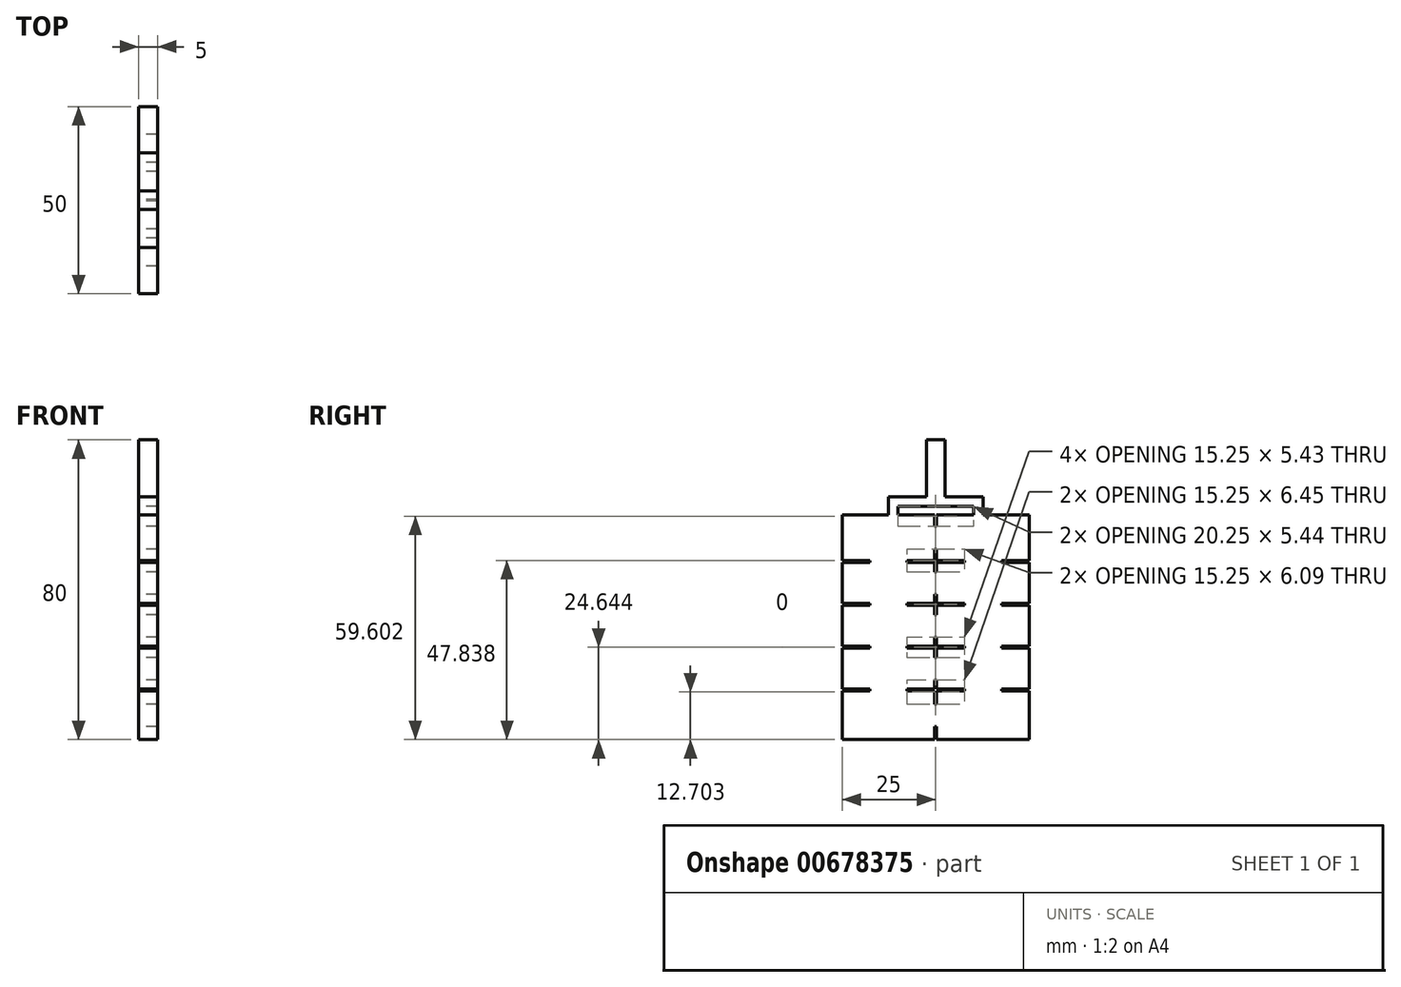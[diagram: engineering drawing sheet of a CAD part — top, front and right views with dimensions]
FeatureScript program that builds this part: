
annotation { "Feature Type Name" : "Feature", "Feature Type Description" : "" }
export const myFeature = defineFeature(function(context is Context, id is Id, definition is map)
    precondition{}
    {
        {
            var Q0;
            Q0=qCreatedBy(makeId("Right.planeOp"),FACE);
            var sketch = newSketch(context, id + "F0", { "sketchPlane" : qUnion([Q0])});
            skPoint(sketch, "E0.0", {"position": v(0, 0) * mm});
            skLineSegment(sketch, "E1.bottom", {"start": v(0, 0) * mm, "end": v(12.38, 0) * mm});
            skLineSegment(sketch, "E1.top", {"start": v(0, -60) * mm, "end": v(24.75, -60) * mm});
            skLineSegment(sketch, "E1.left", {"start": v(0, 0) * mm, "end": v(0, -12.24) * mm});
            skLineSegment(sketch, "E1.right", {"start": v(50, 0) * mm, "end": v(50, -12.24) * mm});
            skPoint(sketch, "E2.MirrorP", {"position": v(11.5, 0) * mm});
            skPoint(sketch, "E3.MirrorP", {"position": v(11.5, -2) * mm});
            skPoint(sketch, "E4.MirrorP", {"position": v(18.5, 0) * mm});
            skPoint(sketch, "E5.MirrorP", {"position": v(30, 0) * mm});
            skLineSegment(sketch, "E6.0", {"start": v(25.25, -60) * mm, "end": v(25.25, -56.52) * mm});
            skLineSegment(sketch, "E7.0", {"start": v(0, -12.24) * mm, "end": v(7.38, -12.24) * mm});
            skLineSegment(sketch, "E8.0", {"start": v(0, -12.74) * mm, "end": v(7.38, -12.74) * mm});
            skLineSegment(sketch, "E9.trimOffspring", {"start": v(25.25, -3.12) * mm, "end": v(25.25, -1.3) * mm});
            skLineSegment(sketch, "E10.trimOffspring", {"start": v(25.25, -12.24) * mm, "end": v(32.63, -12.24) * mm});
            skLineSegment(sketch, "E11.trimOffspring", {"start": v(25.25, -12.24) * mm, "end": v(25.25, -9.12) * mm});
            skLineSegment(sketch, "E12.trimOffspring", {"start": v(25.25, -12.74) * mm, "end": v(32.63, -12.74) * mm});
            skLineSegment(sketch, "E13.trimOffspring", {"start": v(25.25, -15.2) * mm, "end": v(25.25, -12.74) * mm});
            skLineSegment(sketch, "E14.0", {"start": v(0, -23.67) * mm, "end": v(7.38, -23.67) * mm});
            skLineSegment(sketch, "E15.0", {"start": v(0, -24.17) * mm, "end": v(7.38, -24.17) * mm});
            skLineSegment(sketch, "E16.trimOffspring", {"start": v(25.25, -23.67) * mm, "end": v(32.63, -23.67) * mm});
            skLineSegment(sketch, "E17.trimOffspring", {"start": v(25.25, -23.67) * mm, "end": v(25.25, -21.2) * mm});
            skLineSegment(sketch, "E18.trimOffspring", {"start": v(25.25, -24.17) * mm, "end": v(32.63, -24.17) * mm});
            skLineSegment(sketch, "E19.trimOffspring", {"start": v(25.25, -26.64) * mm, "end": v(25.25, -24.17) * mm});
            skLineSegment(sketch, "E20.trimOffspring", {"start": v(24.75, -26.64) * mm, "end": v(24.75, -24.17) * mm});
            skLineSegment(sketch, "E21.0", {"start": v(0, -35.1) * mm, "end": v(7.38, -35.1) * mm});
            skLineSegment(sketch, "E22.0", {"start": v(0, -35.6) * mm, "end": v(7.38, -35.6) * mm});
            skLineSegment(sketch, "E23.trimOffspring", {"start": v(25.25, -35.1) * mm, "end": v(32.63, -35.1) * mm});
            skLineSegment(sketch, "E24.trimOffspring", {"start": v(25.25, -35.1) * mm, "end": v(25.25, -32.64) * mm});
            skLineSegment(sketch, "E25.trimOffspring", {"start": v(24.75, -35.1) * mm, "end": v(24.75, -32.64) * mm});
            skLineSegment(sketch, "E26.trimOffspring", {"start": v(25.25, -35.6) * mm, "end": v(32.63, -35.6) * mm});
            skLineSegment(sketch, "E27.trimOffspring", {"start": v(25.25, -38.07) * mm, "end": v(25.25, -35.6) * mm});
            skLineSegment(sketch, "E28.trimOffspring", {"start": v(24.75, -38.07) * mm, "end": v(24.75, -35.6) * mm});
            skLineSegment(sketch, "E29.0", {"start": v(0, -46.54) * mm, "end": v(7.38, -46.54) * mm});
            skLineSegment(sketch, "E30.0", {"start": v(0, -47.04) * mm, "end": v(7.38, -47.04) * mm});
            skLineSegment(sketch, "E31.trimOffspring", {"start": v(25.25, -46.54) * mm, "end": v(32.63, -46.54) * mm});
            skLineSegment(sketch, "E32.trimOffspring", {"start": v(25.25, -46.54) * mm, "end": v(25.25, -44.07) * mm});
            skLineSegment(sketch, "E33.trimOffspring", {"start": v(24.75, -46.54) * mm, "end": v(24.75, -44.07) * mm});
            skLineSegment(sketch, "E34.trimOffspring", {"start": v(25.25, -47.04) * mm, "end": v(32.63, -47.04) * mm});
            skLineSegment(sketch, "E35.trimOffspring", {"start": v(25.25, -50.52) * mm, "end": v(25.25, -47.04) * mm});
            skLineSegment(sketch, "E36.trimOffspring", {"start": v(0, -12.74) * mm, "end": v(0, -23.67) * mm});
            skLineSegment(sketch, "E37.trimOffspring", {"start": v(0, -24.17) * mm, "end": v(0, -35.1) * mm});
            skLineSegment(sketch, "E38.trimOffspring", {"start": v(0, -35.6) * mm, "end": v(0, -46.54) * mm});
            skLineSegment(sketch, "E39.trimOffspring", {"start": v(0, -47.04) * mm, "end": v(0, -60) * mm});
            skLineSegment(sketch, "E40.trimOffspring", {"start": v(50, -47.04) * mm, "end": v(50, -60) * mm});
            skLineSegment(sketch, "E41.trimOffspring", {"start": v(50, -35.6) * mm, "end": v(50, -46.54) * mm});
            skLineSegment(sketch, "E42.trimOffspring", {"start": v(50, -12.74) * mm, "end": v(50, -23.67) * mm});
            skLineSegment(sketch, "E43.trimOffspring", {"start": v(50, -24.17) * mm, "end": v(50, -35.1) * mm});
            skLineSegment(sketch, "E44.0", {"start": v(17.38, -12.74) * mm, "end": v(17.38, -12.24) * mm});
            skLineSegment(sketch, "E45.0", {"start": v(7.38, -12.74) * mm, "end": v(7.38, -12.24) * mm});
            skLineSegment(sketch, "E46", {"start": v(24.75, -12.24) * mm, "end": v(24.75, -9.12) * mm});
            skLineSegment(sketch, "E47.0", {"start": v(24.75, -9.12) * mm, "end": v(25.25, -9.12) * mm});
            skLineSegment(sketch, "E48.0", {"start": v(24.75, -3.12) * mm, "end": v(25.25, -3.12) * mm});
            skLineSegment(sketch, "E49", {"start": v(24.75, -12.74) * mm, "end": v(24.75, -15.2) * mm});
            skLineSegment(sketch, "E50.0", {"start": v(24.75, -21.2) * mm, "end": v(25.25, -21.2) * mm});
            skLineSegment(sketch, "E51.0", {"start": v(24.75, -15.2) * mm, "end": v(25.25, -15.2) * mm});
            skLineSegment(sketch, "E52", {"start": v(25.25, -1.3) * mm, "end": v(25.25, 0) * mm});
            skLineSegment(sketch, "E53.trimOffspring", {"start": v(25.25, 0) * mm, "end": v(35.12, 0) * mm});
            skPoint(sketch, "E54.start.orphan", {"position": v(24.75, -6.12) * mm});
            skLineSegment(sketch, "E55", {"start": v(7.38, -12.24) * mm, "end": v(7.38, -12.74) * mm});
            skLineSegment(sketch, "E56", {"start": v(17.38, -12.24) * mm, "end": v(17.38, -12.74) * mm});
            skLineSegment(sketch, "E57.trimOffspring", {"start": v(7.38, -23.67) * mm, "end": v(7.38, -24.17) * mm});
            skLineSegment(sketch, "E58.trimOffspring", {"start": v(17.38, -23.67) * mm, "end": v(17.38, -24.17) * mm});
            skLineSegment(sketch, "E59.trimOffspring", {"start": v(7.38, -35.1) * mm, "end": v(7.38, -35.6) * mm});
            skLineSegment(sketch, "E60.trimOffspring", {"start": v(17.38, -35.1) * mm, "end": v(17.38, -35.6) * mm});
            skLineSegment(sketch, "E61.trimOffspring", {"start": v(7.38, -46.54) * mm, "end": v(7.38, -47.04) * mm});
            skLineSegment(sketch, "E62.trimOffspring", {"start": v(17.38, -46.54) * mm, "end": v(17.38, -47.04) * mm});
            skLineSegment(sketch, "E63.trimOffspring", {"start": v(17.38, -46.54) * mm, "end": v(24.75, -46.54) * mm});
            skLineSegment(sketch, "E64.trimOffspring", {"start": v(17.38, -47.04) * mm, "end": v(24.75, -47.04) * mm});
            skLineSegment(sketch, "E65.trimOffspring", {"start": v(17.38, -35.1) * mm, "end": v(24.75, -35.1) * mm});
            skLineSegment(sketch, "E66.trimOffspring", {"start": v(17.38, -35.6) * mm, "end": v(24.75, -35.6) * mm});
            skLineSegment(sketch, "E67.trimOffspring", {"start": v(17.37, -23.67) * mm, "end": v(24.75, -23.67) * mm});
            skLineSegment(sketch, "E68.trimOffspring", {"start": v(17.37, -24.17) * mm, "end": v(24.75, -24.17) * mm});
            skLineSegment(sketch, "E69.trimOffspring", {"start": v(17.38, -12.24) * mm, "end": v(24.75, -12.24) * mm});
            skPoint(sketch, "E70.start.orphan", {"position": v(12.38, -12.74) * mm});
            skPoint(sketch, "E71.orphan", {"position": v(12.38, -12.24) * mm});
            skLineSegment(sketch, "E72.trimOffspring", {"start": v(17.38, -12.74) * mm, "end": v(24.75, -12.74) * mm});
            skLineSegment(sketch, "E73.0", {"start": v(32.63, -12.24) * mm, "end": v(32.63, -12.74) * mm});
            skLineSegment(sketch, "E74.0", {"start": v(42.62, -12.24) * mm, "end": v(42.62, -12.74) * mm});
            skLineSegment(sketch, "E75.trimOffspring", {"start": v(32.63, -23.67) * mm, "end": v(32.63, -24.17) * mm});
            skLineSegment(sketch, "E76.trimOffspring", {"start": v(42.62, -23.67) * mm, "end": v(42.62, -24.17) * mm});
            skLineSegment(sketch, "E77.trimOffspring", {"start": v(32.63, -35.1) * mm, "end": v(32.63, -35.6) * mm});
            skLineSegment(sketch, "E78.trimOffspring", {"start": v(42.62, -35.1) * mm, "end": v(42.62, -35.6) * mm});
            skLineSegment(sketch, "E79.trimOffspring", {"start": v(32.63, -46.54) * mm, "end": v(32.63, -47.04) * mm});
            skLineSegment(sketch, "E80.trimOffspring", {"start": v(42.62, -46.54) * mm, "end": v(42.62, -47.04) * mm});
            skLineSegment(sketch, "E81.0", {"start": v(24.75, -26.64) * mm, "end": v(25.25, -26.64) * mm});
            skLineSegment(sketch, "E82.0", {"start": v(24.75, -32.64) * mm, "end": v(25.25, -32.64) * mm});
            skLineSegment(sketch, "E83.0", {"start": v(24.75, -38.07) * mm, "end": v(25.25, -38.07) * mm});
            skLineSegment(sketch, "E84.0", {"start": v(24.75, -44.07) * mm, "end": v(25.25, -44.07) * mm});
            skLineSegment(sketch, "E85", {"start": v(24.75, -47.04) * mm, "end": v(24.75, -50.52) * mm});
            skLineSegment(sketch, "E86.0", {"start": v(24.75, -56.52) * mm, "end": v(25.25, -56.52) * mm});
            skLineSegment(sketch, "E87.0", {"start": v(24.75, -50.52) * mm, "end": v(25.25, -50.52) * mm});
            skLineSegment(sketch, "E88.trimOffspring", {"start": v(24.75, -56.52) * mm, "end": v(24.75, -60) * mm});
            skLineSegment(sketch, "E89.trimOffspring", {"start": v(25.25, -60) * mm, "end": v(50, -60) * mm});
            skLineSegment(sketch, "E90.trimOffspring", {"start": v(42.62, -46.54) * mm, "end": v(50, -46.54) * mm});
            skLineSegment(sketch, "E91.trimOffspring", {"start": v(42.62, -47.04) * mm, "end": v(50, -47.04) * mm});
            skLineSegment(sketch, "E92.trimOffspring", {"start": v(42.62, -35.1) * mm, "end": v(50, -35.1) * mm});
            skLineSegment(sketch, "E93.trimOffspring", {"start": v(42.62, -35.6) * mm, "end": v(50, -35.6) * mm});
            skLineSegment(sketch, "E94.trimOffspring", {"start": v(42.62, -23.67) * mm, "end": v(50, -23.67) * mm});
            skLineSegment(sketch, "E95.trimOffspring", {"start": v(42.62, -24.17) * mm, "end": v(50, -24.17) * mm});
            skLineSegment(sketch, "E96.trimOffspring", {"start": v(42.62, -12.24) * mm, "end": v(50, -12.24) * mm});
            skLineSegment(sketch, "E97.trimOffspring", {"start": v(42.62, -12.74) * mm, "end": v(50, -12.74) * mm});
            skLineSegment(sketch, "E98.trimOffspring", {"start": v(24.75, -21.2) * mm, "end": v(24.75, -23.67) * mm});
            skPoint(sketch, "E99.end.orphan", {"position": v(25.25, -18.2) * mm});
            skPoint(sketch, "E99.start.orphan", {"position": v(24.75, -18.2) * mm});
            skPoint(sketch, "E100.orphan", {"position": v(25.25, -17.95) * mm});
            skPoint(sketch, "E101.end.orphan", {"position": v(25.25, -18.45) * mm});
            skLineSegment(sketch, "E102.trimOffspring", {"start": v(24.75, -3.12) * mm, "end": v(24.75, 0) * mm});
            skLineSegment(sketch, "E103", {"start": v(12.38, 0) * mm, "end": v(12.38, 4.82) * mm});
            skLineSegment(sketch, "E104.0", {"start": v(14.88, 0) * mm, "end": v(14.88, 2.32) * mm});
            skLineSegment(sketch, "E105", {"start": v(37.63, 0) * mm, "end": v(37.63, 4.82) * mm});
            skLineSegment(sketch, "E106.0", {"start": v(35.12, 0) * mm, "end": v(35.12, 2.32) * mm});
            skLineSegment(sketch, "E107.0", {"start": v(27.5, 9.82) * mm, "end": v(27.5, 20) * mm});
            skLineSegment(sketch, "E108.0", {"start": v(22.5, 9.82) * mm, "end": v(22.5, 20) * mm});
            skPoint(sketch, "E109.orphan", {"position": v(14.88, 25) * mm});
            skPoint(sketch, "E110.orphan", {"position": v(37.63, 25) * mm});
            skLineSegment(sketch, "E111.trimOffspring", {"start": v(14.88, 0) * mm, "end": v(24.75, 0) * mm});
            skLineSegment(sketch, "E112.trimOffspring", {"start": v(37.63, 0) * mm, "end": v(50, 0) * mm});
            skLineSegment(sketch, "E113.0", {"start": v(14.88, 2.32) * mm, "end": v(35.12, 2.32) * mm});
            skLineSegment(sketch, "E114.0", {"start": v(12.38, 4.82) * mm, "end": v(22.5, 4.82) * mm});
            skLineSegment(sketch, "E115.0", {"start": v(27.5, 4.82) * mm, "end": v(37.63, 4.82) * mm});
            skLineSegment(sketch, "E116", {"start": v(22.5, 9.82) * mm, "end": v(22.5, 4.82) * mm});
            skLineSegment(sketch, "E117", {"start": v(27.5, 4.82) * mm, "end": v(27.5, 9.82) * mm});
            skLineSegment(sketch, "E118.0", {"start": v(22.5, 20) * mm, "end": v(27.5, 20) * mm});
            skSolve(sketch);
        }
        {
            var Q0;
            {var subQ1=sQuery(id+"F0.wireOp",EDGE,"6f222dcf-cafe-427f-96f1-de862232ba62.0");Q0=makeQuery(id+"F0.imprint","IMPRINT",FACE,{"disambiguationData":[TD([[makeQuery(id+"F0.imprint","IMPRINT",EDGE,{"derivedFrom":subQ1}),-1.0]])]});}
            var Q1;
            {var subQ1=sQuery(id+"F0.wireOp",EDGE,"9ddca581-0f96-48d2-9b8e-d0e5be099db1.trimOffspring");Q1=makeQuery(id+"F0.imprint","IMPRINT",FACE,{"disambiguationData":[TD([[makeQuery(id+"F0.imprint","IMPRINT",EDGE,{"derivedFrom":subQ1}),-1.0]])]});}
            var Q2;
            Q2=makeQuery(id+"F0.imprint","IMPRINT",FACE,{"disambiguationData":[TD([[makeQuery(id+"F0.imprint","IMPRINT",EDGE,{"derivedFrom":sQuery(id+"F0.wireOp",EDGE,"E8.0")}),-1.0]])]});
            var Q3;
            Q3=makeQuery(id+"F0.imprint","IMPRINT",FACE,{"disambiguationData":[TD([[makeQuery(id+"F0.imprint","IMPRINT",EDGE,{"derivedFrom":sQuery(id+"F0.wireOp",EDGE,"E12.trimOffspring")}),-1.0]])]});
            var Q4;
            Q4=makeQuery(id+"F0.imprint","IMPRINT",FACE,{"disambiguationData":[TD([[makeQuery(id+"F0.imprint","IMPRINT",EDGE,{"derivedFrom":sQuery(id+"F0.wireOp",EDGE,"E18.trimOffspring")}),-1.0]])]});
            var Q5;
            Q5=makeQuery(id+"F0.imprint","IMPRINT",FACE,{"disambiguationData":[TD([[makeQuery(id+"F0.imprint","IMPRINT",EDGE,{"derivedFrom":sQuery(id+"F0.wireOp",EDGE,"E15.0")}),-1.0]])]});
            var Q6;
            Q6=makeQuery(id+"F0.imprint","IMPRINT",FACE,{"disambiguationData":[TD([[makeQuery(id+"F0.imprint","IMPRINT",EDGE,{"derivedFrom":sQuery(id+"F0.wireOp",EDGE,"E22.0")}),-1.0]])]});
            var Q7;
            Q7=makeQuery(id+"F0.imprint","IMPRINT",FACE,{"disambiguationData":[TD([[makeQuery(id+"F0.imprint","IMPRINT",EDGE,{"derivedFrom":sQuery(id+"F0.wireOp",EDGE,"E26.trimOffspring")}),-1.0]])]});
            var Q8;
            {var subQ0=sQuery(id+"F0.wireOp",EDGE,"E6.0");Q8=makeQuery(id+"F0.imprint","IMPRINT",FACE,{"disambiguationData":[TD([[makeQuery(id+"F0.imprint","IMPRINT",EDGE,{"derivedFrom":subQ0}),-1.0]])]});}
            var Q9;
            {var subQ0=sQuery(id+"F0.wireOp",EDGE,"52d86100-12cc-4532-affd-39e9c9b04a49.0");Q9=makeQuery(id+"F0.imprint","IMPRINT",FACE,{"disambiguationData":[TD([[makeQuery(id+"F0.imprint","IMPRINT",EDGE,{"derivedFrom":subQ0}),1.0]])]});}
            extrude(context, id + "F1", {"entities" : qUnion([Q0, Q1, Q2, Q3, Q4, Q5, Q6, Q7, Q8, Q9]), "depth" : 5 * mm, "offsetDistance" : 25 * mm});
        }
    });
